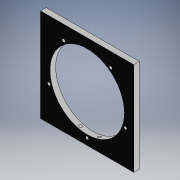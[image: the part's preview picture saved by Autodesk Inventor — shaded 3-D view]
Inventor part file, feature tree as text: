
AUTODESK INVENTOR PART (.ipt)
format: ipt  version: 2019 (Build 230136000, 136)  size: 146,432 bytes
history: native  units: mm
features: sketch x4, extrude x2, hole x2
ambient origin geometry x8: Origin, YZ Plane, XZ Plane, XY Plane, X Axis, Y Axis, Z Axis, Center Point
bodies: Solid1 (feature_tree)
feature tree (8):
  extrude  "Extrusion1"  Depth=158.0mm
  hole  "Hole1"  [1 undecoded]
  extrude  "Extrusion2"  Depth=126.0mm
  hole  "Hole2"  [1 undecoded]
  sketch  "Sketch1"  dims[d0=158.0mm d1=158.0mm]
  sketch  "Sketch2"  dims[d2=9.525mm d3=0.0mm d4=136.0mm]
  sketch  "Sketch4"  dims[d5=50.0mm d7=360.0deg]
  sketch  "Sketch5"  dims[d9=5.0mm d10=6.0mm d11=11.113mm d12=6.35mm d13=90.0deg d14=8.0mm d15=20.594885mm d16=126.0mm d17=12.7mm d18=0.0mm d19=31.6mm d20=31.6mm d21=31.6mm d22=31.6mm d23=31.6mm d24=4.978mm d25=9.525mm d26=11.113mm d27=6.35mm d28=90.0deg d29=19.05mm d30=20.594885mm]
note: 2 required parameter values undecoded (feature->parameter linkage not recoverable at this tier; creation-order binding heuristic only, values carry confidence <= 0.55)
